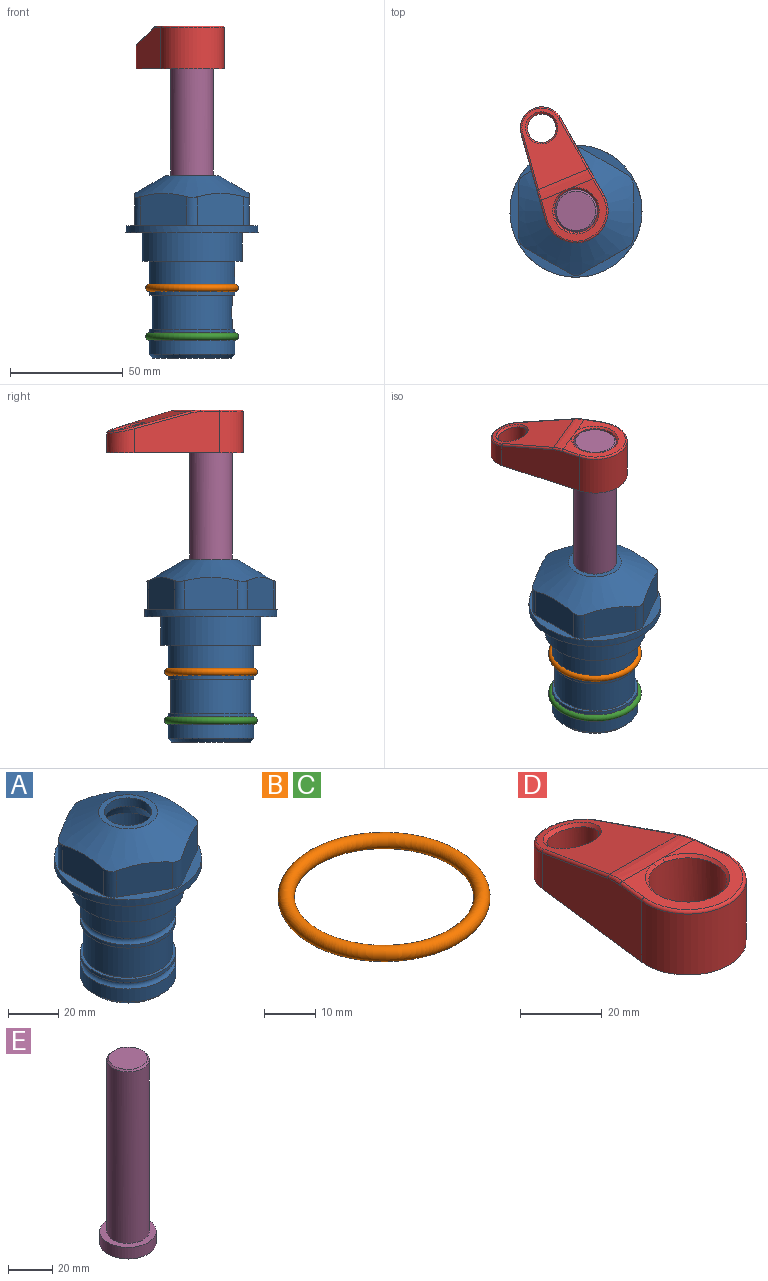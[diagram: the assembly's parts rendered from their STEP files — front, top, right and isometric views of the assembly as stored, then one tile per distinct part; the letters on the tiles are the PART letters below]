
ASSEMBLY  parts=5 mates=3
PART A: 36 faces, bbox 58.7x58.7x81 mm
  f0: cylinder r=17.78mm len=35.56mm, axis (0,0,1), area 1670.8mm2, adj f23,f24,f31
  f1: cylinder r=19.05mm len=38.1mm, axis (0,0,1), area 1191.9mm2, adj f26,f27,f30
  f2: plane 58.66x58.66mm, normal (0,0,-1), area 1150.6mm2, adj f3,f28
  f3: cylinder r=29.33mm len=58.66mm, axis (0,0,-1), area 585.1mm2, adj f2,f4
  f4: plane 58.66x58.66mm, normal (0,0,1), area 475.9mm2, adj f3,f5,f6,f7,f8,f9,f10,f11
  f5: plane 20.32x14.34mm, normal (-0.5,0.87,0), area 324.4mm2, adj f4,f15,f16,f17
  f6: plane 20.32x14.34mm, normal (0.5,0.87,0), area 324.4mm2, adj f4,f14,f15,f17
  f7: plane 23.48x14.34mm, normal (1,0,0), area 324.4mm2, adj f4,f13,f14,f17
  f8: plane 20.32x14.34mm, normal (0.5,-0.87,0), area 324.4mm2, adj f4,f12,f13,f17
  f9: plane 20.32x14.34mm, normal (-0.5,-0.87,0), area 324.4mm2, adj f4,f11,f12,f17
  f10: plane 23.48x14.34mm, normal (-1,0,0), area 324.4mm2, adj f4,f11,f16,f17
  f11: cylinder r=5.08mm len=12.85mm, axis (0,0,-1), area 67.2mm2, adj f4,f9,f10,f17
  f12: cylinder r=5.08mm len=12.85mm, axis (0,0,-1), area 67.2mm2, adj f4,f8,f9,f17
  f13: cylinder r=5.08mm len=12.85mm, axis (0,0,-1), area 67.2mm2, adj f4,f7,f8,f17
  f14: cylinder r=5.08mm len=12.85mm, axis (0,0,-1), area 67.2mm2, adj f4,f6,f7,f17
  f15: cylinder r=5.08mm len=12.85mm, axis (0,0,-1), area 67.2mm2, adj f4,f5,f6,f17
  f16: cylinder r=5.08mm len=12.85mm, axis (0,0,-1), area 67.2mm2, adj f4,f5,f10,f17
  f17: cone r=11.73mm half-angle=60deg, axis (0,0,-1), area 2071.8mm2, adj f5,f6,f7,f8,f9,f10,f11,f12
  f18: plane 23.46x23.46mm, normal (0,0,1), area 147.4mm2, adj f17,f35
  f19: plane 34.93x34.93mm, normal (0,0,-1), area 958mm2, adj f29
  f20: cylinder r=19.05mm len=38.1mm, axis (0,0,1), area 760.1mm2, adj f21,f29
  f21: torus R=19.05mm, axis (0,0,1), area 565.3mm2, adj f20,f22
  f22: cylinder r=19.05mm len=38.1mm, axis (0,0,1), area 190mm2, adj f21,f23
  f23: plane 38.1x38.1mm, normal (0,0,1), area 146.9mm2, adj f0,f22
  f24: plane 38.1x38.1mm, normal (0,0,-1), area 146.9mm2, adj f0,f25
  f25: cylinder r=19.05mm len=38.1mm, axis (0,0,1), area 190mm2, adj f24,f26
  f26: torus R=19.05mm, axis (0,0,1), area 565.3mm2, adj f1,f25
  f27: plane 44.45x44.45mm, normal (0,0,-1), area 411.7mm2, adj f1,f28
  f28: cylinder r=22.23mm len=44.45mm, axis (0,0,1), area 1773.5mm2, adj f2,f27
  f29: cone r=19.05mm half-angle=45deg, axis (0,0,1), area 257.5mm2, adj f19,f20
  f30: cylinder r=3.17mm len=6.75mm, axis (-1,0,0), area 128mm2, adj f1,f33
  f31: cylinder r=3.17mm len=6.35mm, axis (-1,0,0), area 102.5mm2, adj f0,f33
  f32: plane 25.4x25.4mm, normal (0,0,1), area 506.7mm2, adj f33
  f33: cylinder r=12.7mm len=66.42mm, axis (0,0,-1), area 5236.2mm2, adj f30,f31,f32,f34
  f34: cone r=9.53mm half-angle=30deg, axis (0,0,-1), area 443.4mm2, adj f33,f35
  f35: cylinder r=9.53mm len=19.05mm, axis (0,0,-1), area 240.9mm2, adj f18,f34
PART B: 1 faces, bbox 44.7x44.7x3.2 mm
  f0: torus R=19.05mm, axis (0,0,1), area 1193.9mm2
PART C: same geometry as B
PART D: 31 faces, bbox 31.7x65.5x19.8 mm
  f0: plane 39.12x18.26mm, normal (0.99,0.12,0), area 612.2mm2, adj f1,f4,f7,f11,f13,f15
  f1: cylinder r=9.53mm len=18.91mm, axis (0,0,-1), area 296.1mm2, adj f0,f2,f7,f17
  f2: plane 39.12x18.26mm, normal (-0.99,0.12,0), area 612.2mm2, adj f1,f4,f7,f12,f14,f16
  f3: cylinder r=6.35mm len=12.7mm, axis (0,0,-1), area 362.4mm2, adj f7,f18
  f4: cylinder r=14.29mm len=28.58mm, axis (0,0,-1), area 882.2mm2, adj f0,f2,f7,f10
  f5: cylinder r=9.53mm len=19.05mm, axis (0,0,-1), area 1092.6mm2, adj f7,f19,f20
  f6: plane 26.99x23.69mm, normal (0,0,1), area 216.2mm2, adj f9,f10,f11,f12,f19
  f7: plane 63.5x28.58mm, normal (0,0,-1), area 661.8mm2, adj f0,f1,f2,f3,f4,f5,f22,f23
  f8: plane 33.52x23.6mm, normal (0,0.26,0.97), area 486mm2, adj f9,f15,f16,f17,f18
  f9: cylinder r=19.05mm len=24.72mm, axis (1,0,0), area 120.4mm2, adj f6,f8,f13,f14,f20
  f10: torus R=13.49mm, axis (0,0,1), area 59mm2, adj f4,f6,f11,f12
  f11: cylinder r=0.79mm len=8.67mm, axis (0.12,-0.99,0), area 10.8mm2, adj f0,f6,f10,f13
  f12: cylinder r=0.79mm len=8.67mm, axis (0.12,0.99,0), area 10.8mm2, adj f2,f6,f10,f14
  f13: bspline ~4.95x1.42mm, area 6.1mm2, adj f0,f9,f11,f15
  f14: bspline ~4.95x1.42mm, area 6.1mm2, adj f2,f9,f12,f16
  f15: cylinder r=0.79mm len=25.95mm, axis (0.12,-0.96,0.26), area 32.9mm2, adj f0,f8,f13,f17
  f16: cylinder r=0.79mm len=25.95mm, axis (0.12,0.96,-0.26), area 32.9mm2, adj f2,f8,f14,f17
  f17: bspline ~18.91x8.38mm, area 30mm2, adj f1,f8,f15,f16
  f18: bspline ~14.29x14.29mm, area 48.3mm2, adj f3,f8
  f19: cone r=9.53mm half-angle=45deg, axis (0,0,1), area 66.5mm2, adj f5,f6,f20
  f20: bspline ~3.22x0.96mm, area 3.5mm2, adj f5,f9,f19
  f21: plane 2.75x2.72mm, normal (0,0,-1), area 2.9mm2, adj f23,f25,f28
  f22: plane 23.05x15.88mm, normal (-0.99,-0.12,0), area 323.6mm2, adj f7,f25,f26,f27,f28,f29
  f23: plane 23.05x15.88mm, normal (0.99,-0.12,0), area 323.6mm2, adj f7,f21,f25,f27,f28,f30
  f24: cylinder r=9.53mm len=10.69mm, axis (0,0,-1), area 114.7mm2, adj f7,f27,f29,f30
  f25: cylinder r=12.7mm len=20.59mm, axis (0,0,-1), area 381.1mm2, adj f7,f21,f22,f23,f26,f28
  f26: plane 2.75x2.72mm, normal (0,0,-1), area 2.9mm2, adj f22,f25,f28
  f27: plane 19.72x18.37mm, normal (0,-0.26,-0.97), area 291.8mm2, adj f22,f23,f24,f28,f29,f30
  f28: cylinder r=15.88mm len=19.92mm, axis (1,0,0), area 54.8mm2, adj f21,f22,f23,f25,f26,f27
  f29: cylinder r=1.59mm len=11mm, axis (0,0,-1), area 34.7mm2, adj f7,f22,f24,f27
  f30: cylinder r=1.59mm len=11mm, axis (0,0,-1), area 34.7mm2, adj f7,f23,f24,f27
PART E: 6 faces, bbox 25.4x25.4x101.6 mm
  f0: plane 17.46x17.46mm, normal (0,0,1), area 239.5mm2, adj f5
  f1: plane 25.4x25.4mm, normal (0,0,-1), area 506.7mm2, adj f2
  f2: cylinder r=12.7mm len=25.4mm, axis (0,0,1), area 506.7mm2, adj f1,f3
  f3: plane 25.4x25.4mm, normal (0,0,1), area 221.7mm2, adj f2,f4
  f4: cylinder r=9.53mm len=94.46mm, axis (0,0,1), area 5653mm2, adj f3,f5
  f5: cone r=8.73mm half-angle=45deg, axis (0,0,-1), area 64.4mm2, adj f0,f4
PLACE A at identity fixed
PLACE B at identity
PLACE C t=(0,0,-21.59)mm
PLACE D rot(axis=(0,0,1),22.5deg) t=(0,0,28.35)mm
PLACE E rot(axis=(0,0,1),22.5deg) t=(0,0,27.55)mm
MATE fastened D.f4 <-> E.f2  axis (0,0,-1) through (0,0,91.05)mm
MATE cylindrical A.f0 <-> E.f2  axis (0,0,1) through (0,0,-50.55)mm
MATE fastened C.f0 <-> A.f0  axis (0,0,1) through (0,0,-46.1)mm
